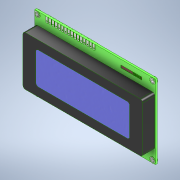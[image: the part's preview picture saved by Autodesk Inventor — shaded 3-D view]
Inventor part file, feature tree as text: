
AUTODESK INVENTOR PART (.ipt)
format: ipt  version: 2021 (Build 250183000, 183)  size: 710,656 bytes
history: native  units: mm
features: extrude x7, sketch x7, projected_geometry x2
ambient origin geometry x8: Origin, YZ Plane, XZ Plane, XY Plane, X Axis, Y Axis, Z Axis, Center Point
bodies: Solid1 (feature_tree), Solid3 (feature_tree)
feature tree (16):
  extrude  "Extrusion1"  Depth=60.0mm
  extrude  "Extrusion3"  Depth=3.3mm
  extrude  "Extrusion4"  Depth=3.3mm
  extrude  "Extrusion5"  Depth=10.0mm
  extrude  "Extrusion7"  Depth=1.0mm
  extrude  "Extrusion8"  Depth=1.0mm
  extrude  "Extrusion9"  Depth=0.2mm
  sketch  "Sketch1"  dims[d0=97.9mm d1=60.0mm]
  sketch  "Sketch4"  dims[d3=3.3mm d4=3.3mm]
  projected_geometry  "Projected Loop3"
  sketch  "Sketch5"  dims[d5=3.3mm d6=3.3mm]
  sketch  "Sketch6"  dims[d7=1.5mm d8=0.0mm d11=10.0mm]
  sketch  "Sketch9"  dims[d12=3.0mm d15=1.0mm]
  projected_geometry  "Projected Loop5"
  sketch  "Sketch10"  dims[d16=1.0mm d17=0.64mm]
  sketch  "Sketch11"  dims[d18=0.64mm d20=0.64mm d21=0.64mm d23=0.64mm d24=0.64mm d26=0.64mm d27=0.64mm d29=0.64mm d30=0.64mm d32=0.64mm d33=0.64mm d35=0.64mm d36=0.64mm d38=0.64mm d39=0.64mm d41=0.64mm d42=0.64mm d44=0.64mm d45=0.64mm d47=0.64mm d48=0.64mm d50=0.64mm d51=0.64mm d53=0.64mm d54=0.64mm d56=0.64mm d57=0.64mm d59=0.64mm d60=0.64mm d62=0.64mm d63=0.64mm d64=1.0mm d65=1.0mm d67=1.0mm d68=1.0mm d69=1.0mm d70=1.0mm d71=1.0mm d72=1.0mm d73=1.0mm d74=1.0mm d75=1.0mm d76=1.0mm d77=1.0mm d78=1.0mm d79=1.0mm d80=1.0mm d81=1.0mm d82=1.0mm d83=1.0mm d84=1.0mm d85=1.0mm d86=1.0mm d87=1.0mm d88=1.0mm d89=1.0mm d90=1.0mm d91=1.0mm d92=1.0mm d93=1.0mm d94=1.0mm d95=1.0mm d96=1.0mm d97=0.25mm d98=1.75mm d99=0.0mm d100=0.0mm d101=97.0mm d102=40.0mm d103=2.0mm d104=10.0mm d105=0.0mm d106=76.0mm d107=26.0mm d108=2.0mm d109=5.0mm d110=0.0mm d113=1.0mm d114=0.0mm d117=17.0mm d118=2.1mm d119=0.2mm d120=0.0mm d121=0.2mm d122=0.0mm]
